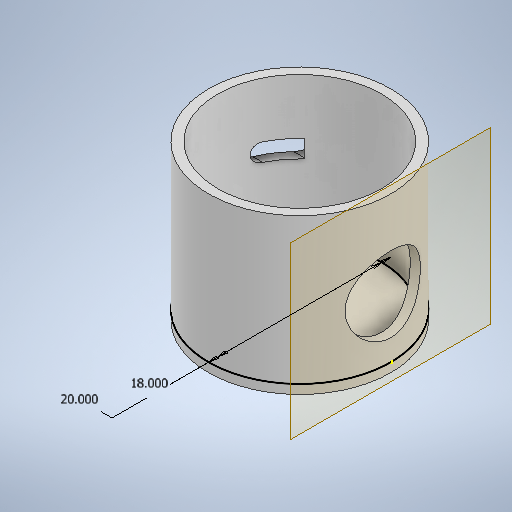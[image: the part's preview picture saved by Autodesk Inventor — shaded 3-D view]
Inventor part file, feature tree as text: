
AUTODESK INVENTOR PART (.ipt)
format: ipt  version: 2025.1 (Build 291241020, 241B)  size: 276,480 bytes
history: native  units: in
note: dims shown in document units (in); Inventor stores cm internally (conversion verified against a paired STEP export)
features: sketch x5, extrude x4, plane x1, other x1
ambient origin geometry x8: Origin, YZ Plane, XZ Plane, XY Plane, X Axis, Y Axis, Z Axis, Center Point
bodies: Solid1 (feature_tree)
feature tree (11):
  extrude  "Extrusion1"  Depth=20.0in
  extrude  "Extrusion2"  Depth=1.0in TaperAngle=0.0deg
  plane  "Work Plane1"
  extrude  "Extrusion3"  Depth=3.0in TaperAngle=0.0deg
  other  "Plane for hole making"
  sketch  "Sketch4"  dims[d10=0.5in d11=0.0344in]
  extrude  "Extrusion4"  Depth=0.0344in
  sketch  "Sketch1"  dims[d0=18.0in d1=20.0in]
  sketch  "Sketch2"  dims[d2=16.0in d3=0.0in d4=1.0in d5=0.0in]
  sketch  "Sketch3"  dims[d6=3.875in d7=0.0in d8=3.0in d9=0.0in]
  sketch  "Sketch5"
